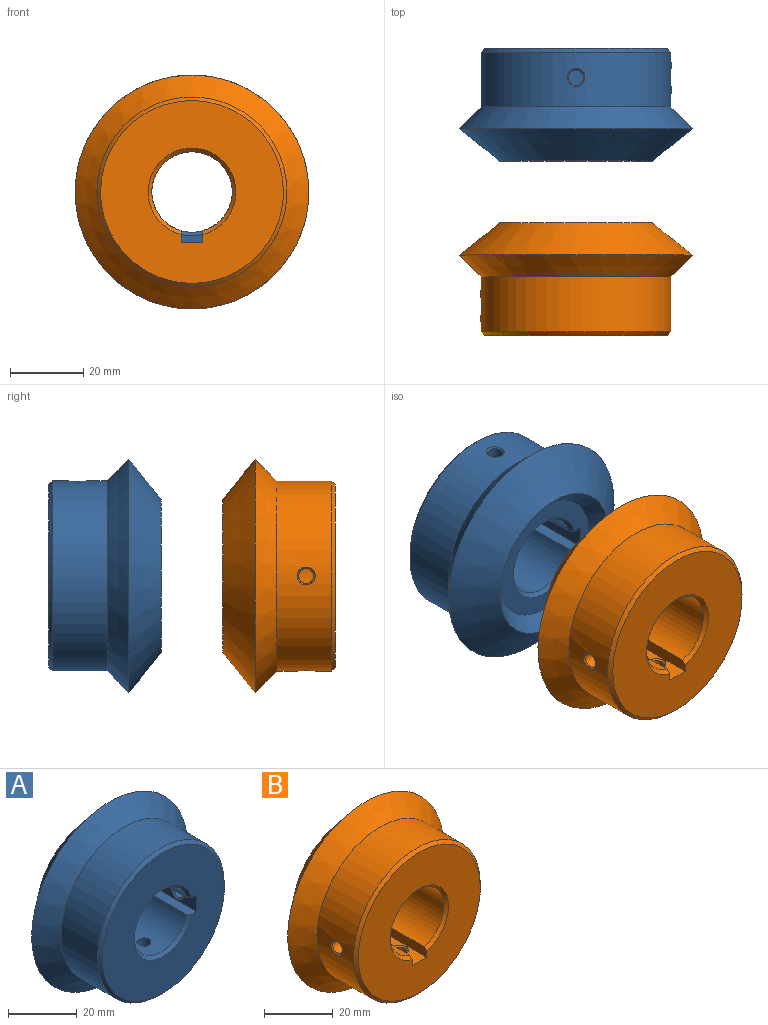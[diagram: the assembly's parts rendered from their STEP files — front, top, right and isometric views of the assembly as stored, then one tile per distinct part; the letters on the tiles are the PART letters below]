
ASSEMBLY  parts=2 mates=1
PART A: 18 faces, bbox 64x30.8x64 mm
  f0: cylinder r=26mm len=52mm, axis (0,-1,0), area 2413.1mm2, adj f6,f7,f10,f17
  f1: cylinder r=11mm len=25mm, axis (0,-1,0), area 1562.4mm2, adj f2,f3,f11,f12,f14
  f2: cone r=12mm half-angle=45deg, axis (0,1,0), area 93.6mm2, adj f1,f5,f12,f14
  f3: cone r=11mm half-angle=45deg, axis (0,-1,0), area 93.6mm2, adj f1,f4,f12,f14
  f4: plane 50x50mm, normal (0,-1,0), area 1499.5mm2, adj f3,f6,f12,f13,f14
  f5: plane 34.4x34.4mm, normal (0,1,0), area 465.7mm2, adj f2,f9,f12,f13,f14
  f6: cone r=25mm half-angle=45deg, axis (0,1,0), area 226.6mm2, adj f0,f4
  f7: cone r=26mm half-angle=45deg, axis (0,1,0), area 1544.1mm2, adj f0,f8
  f8: cone r=32mm half-angle=51.4deg, axis (0,-1,0), area 2344.9mm2, adj f7,f9
  f9: cone r=20.98mm half-angle=45deg, axis (0,1,0), area 641.5mm2, adj f5,f8
  f10: cone r=2.5mm half-angle=45deg, axis (0,0,-1), area 8.5mm2, adj f0,f11
  f11: cylinder r=2.07mm len=14.76mm, axis (0,0,1), area 190.5mm2, adj f1,f10
  f12: plane 27.01x3.23mm, normal (0,0,-1), area 85.8mm2, adj f1,f2,f3,f4,f5,f13
  f13: plane 27x6mm, normal (-1,0,0), area 142.4mm2, adj f4,f5,f12,f14,f15
  f14: plane 27.01x3.23mm, normal (0,0,1), area 85.8mm2, adj f1,f2,f3,f4,f5,f13
  f15: cone r=2.5mm half-angle=45deg, axis (-1,0,0), area 8.8mm2, adj f13,f16
  f16: cylinder r=2.07mm len=11.33mm, axis (1,0,0), area 147.2mm2, adj f15,f17
  f17: cone r=2.07mm half-angle=45deg, axis (1,0,0), area 7mm2, adj f0,f16
PART B: 18 faces, bbox 64x30.8x64 mm
  f0: cylinder r=26mm len=52mm, axis (0,-1,0), area 2413.1mm2, adj f6,f7,f11,f17
  f1: cylinder r=11mm len=25mm, axis (0,-1,0), area 1562.4mm2, adj f2,f3,f10,f12,f13
  f2: cone r=12mm half-angle=45deg, axis (0,1,0), area 93.6mm2, adj f1,f5,f12,f13
  f3: cone r=11mm half-angle=45deg, axis (0,-1,0), area 93.6mm2, adj f1,f4,f12,f13
  f4: plane 50x50mm, normal (0,-1,0), area 1499.5mm2, adj f3,f6,f12,f13,f14
  f5: plane 34.4x34.4mm, normal (0,1,0), area 465.7mm2, adj f2,f9,f12,f13,f14
  f6: cone r=25mm half-angle=45deg, axis (0,1,0), area 226.6mm2, adj f0,f4
  f7: cone r=26mm half-angle=45deg, axis (0,1,0), area 1544.1mm2, adj f0,f8
  f8: cone r=32mm half-angle=51.4deg, axis (0,-1,0), area 2344.9mm2, adj f7,f9
  f9: cone r=20.98mm half-angle=45deg, axis (0,1,0), area 641.5mm2, adj f5,f8
  f10: cylinder r=2.07mm len=14.76mm, axis (-1,0,0), area 191.7mm2, adj f1,f11
  f11: cone r=2.07mm half-angle=45deg, axis (-1,0,0), area 7mm2, adj f0,f10
  f12: plane 27.01x3.23mm, normal (1,0,0), area 85.8mm2, adj f1,f2,f3,f4,f5,f14
  f13: plane 27.01x3.23mm, normal (-1,0,0), area 85.8mm2, adj f1,f2,f3,f4,f5,f14
  f14: plane 27x6mm, normal (0,0,1), area 142.4mm2, adj f4,f5,f12,f13,f15
  f15: cone r=2.5mm half-angle=45deg, axis (0,0,1), area 8.8mm2, adj f14,f16
  f16: cylinder r=2.07mm len=11.33mm, axis (0,0,-1), area 147.2mm2, adj f15,f17
  f17: cone r=2.07mm half-angle=45deg, axis (0,0,-1), area 8.2mm2, adj f0,f16
PLACE A rot(axis=(-1,0,0),180deg) t=(-77.04,123.87,60.27)mm
PLACE B rot(axis=(0.96,0.01,-0.29),0deg) t=(-77.04,45.37,60.27)mm
MATE cylindrical A.f0 <-> B.f0  axis (0,-1,0) through (-77.04,96.87,60.27)mm
